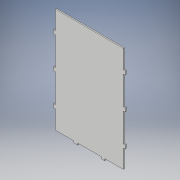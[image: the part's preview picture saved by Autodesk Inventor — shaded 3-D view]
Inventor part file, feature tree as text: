
AUTODESK INVENTOR PART (.ipt)
format: ipt  version: 2018 (Build 220112000, 112)  size: 138,240 bytes
history: native  units: in
note: dims shown in document units (in); Inventor stores cm internally (conversion verified against a paired STEP export)
features: extrude x1, sketch x1
ambient origin geometry x8: Origin, YZ Plane, XZ Plane, XY Plane, X Axis, Y Axis, Z Axis, Center Point
bodies: Solid1 (feature_tree)
feature tree (2):
  extrude  "Extrusion1"  Depth=8.5in
  sketch  "Sketch1"  dims[d0=5.5in d1=8.5in d2=0.3in d3=0.15in d4=0.3in d5=0.15in d6=1.5in d7=1.5in d8=0.15in d9=0.3in d10=0.15in d11=0.3in d12=0.15in d13=0.3in d14=1.5in d15=1.5in d16=2.3in d17=0.1in d18=0.0in]
